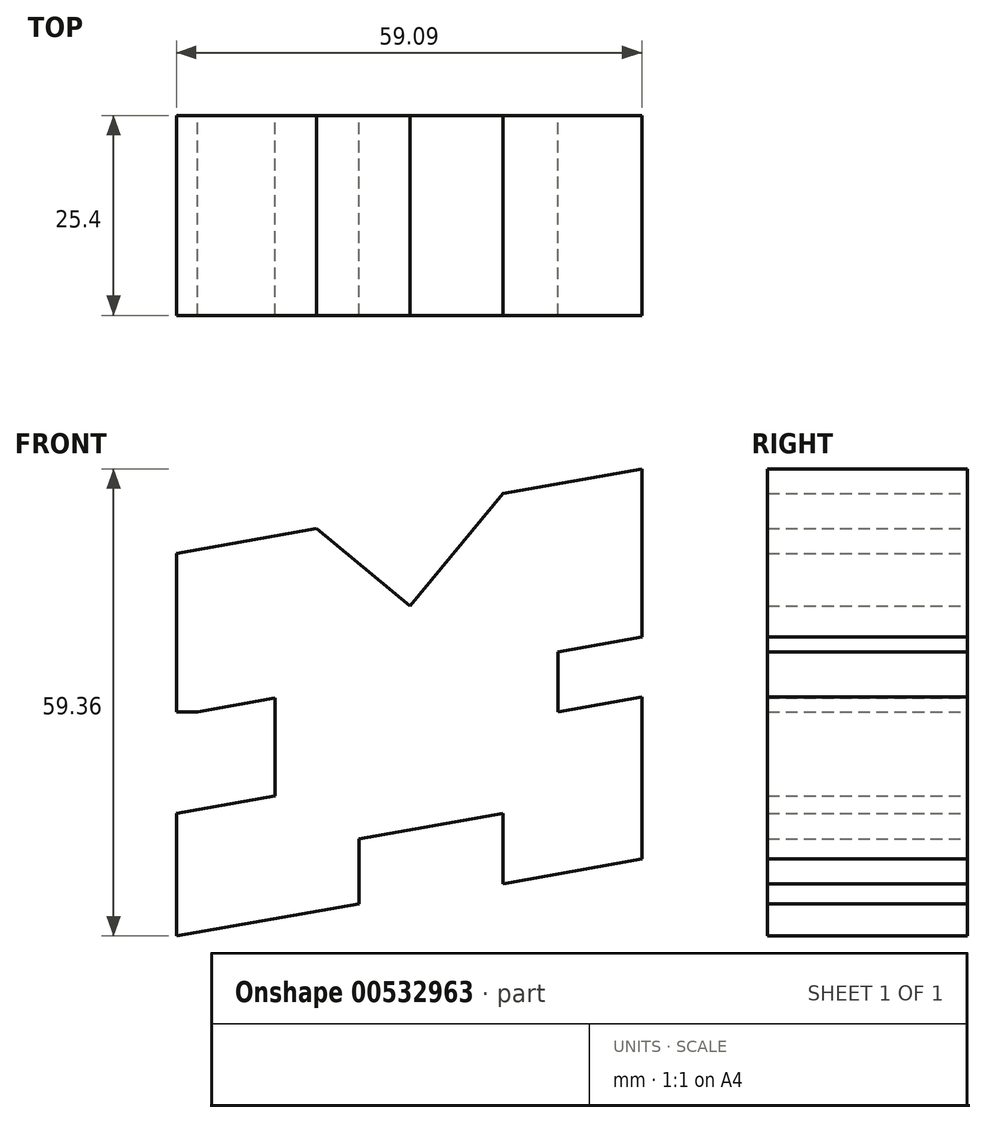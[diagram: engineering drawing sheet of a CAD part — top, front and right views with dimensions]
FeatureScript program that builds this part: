
annotation { "Feature Type Name" : "Feature", "Feature Type Description" : "" }
export const myFeature = defineFeature(function(context is Context, id is Id, definition is map)
    precondition{}
    {
        {
            var Q0;
            Q0=qCreatedBy(makeId("Front.planeOp"),FACE);
            var sketch = newSketch(context, id + "F0", { "sketchPlane" : qUnion([Q0])});
            skLineSegment(sketch, "E0", {"start": v(-29.68, 16.16) * mm, "end": v(-11.87, 19.33) * mm});
            skLineSegment(sketch, "E1", {"start": v(-11.87, 19.33) * mm, "end": v(0, 9.51) * mm});
            skLineSegment(sketch, "E2", {"start": v(0, 9.51) * mm, "end": v(11.78, 23.77) * mm});
            skLineSegment(sketch, "E3", {"start": v(11.78, 23.77) * mm, "end": v(29.41, 26.9) * mm});
            skLineSegment(sketch, "E4", {"start": v(-29.68, 16.16) * mm, "end": v(-29.68, -3.96) * mm});
            skLineSegment(sketch, "E5", {"start": v(29.41, 23.77) * mm, "end": v(29.41, 5.55) * mm});
            skLineSegment(sketch, "E6", {"start": v(-27.04, -3.96) * mm, "end": v(-17.17, -2.2) * mm});
            skLineSegment(sketch, "E7", {"start": v(-17.17, -2.2) * mm, "end": v(-17.17, -14.66) * mm});
            skLineSegment(sketch, "E8", {"start": v(-17.17, -14.66) * mm, "end": v(-29.68, -16.88) * mm});
            skLineSegment(sketch, "E9", {"start": v(-29.68, -16.88) * mm, "end": v(-29.68, -32.46) * mm});
            skLineSegment(sketch, "E10", {"start": v(-29.68, -32.46) * mm, "end": v(-6.52, -28.34) * mm});
            skLineSegment(sketch, "E11", {"start": v(29.41, 5.55) * mm, "end": v(18.75, 3.66) * mm});
            skLineSegment(sketch, "E12", {"start": v(18.75, 3.66) * mm, "end": v(18.75, -3.96) * mm});
            skLineSegment(sketch, "E13", {"start": v(18.75, -3.96) * mm, "end": v(29.41, -2.06) * mm});
            skLineSegment(sketch, "E14", {"start": v(29.41, -2.06) * mm, "end": v(29.41, -16.88) * mm});
            skLineSegment(sketch, "E15", {"start": v(29.41, -16.88) * mm, "end": v(29.41, -22.66) * mm});
            skPoint(sketch, "E15.endSnap0", {"position": v(29.41, -9.47) * mm});
            skLineSegment(sketch, "E16", {"start": v(29.41, -22.66) * mm, "end": v(11.78, -25.8) * mm});
            skLineSegment(sketch, "E17", {"start": v(11.78, -25.8) * mm, "end": v(11.78, -16.88) * mm});
            skLineSegment(sketch, "E18", {"start": v(11.78, -16.88) * mm, "end": v(-6.52, -20.13) * mm});
            skLineSegment(sketch, "E19", {"start": v(-6.52, -20.13) * mm, "end": v(-6.52, -28.34) * mm});
            skLineSegment(sketch, "E20", {"start": v(-27.04, -3.96) * mm, "end": v(-29.68, -3.96) * mm});
            skLineSegment(sketch, "E21", {"start": v(29.41, 26.9) * mm, "end": v(29.41, 19.33) * mm});
            skSolve(sketch);
        }
        {
            var Q0;
            Q0=makeQuery(id+"F0.imprint","IMPRINT",FACE,{"disambiguationData":[TD([[makeQuery(id+"F0.imprint","IMPRINT",EDGE,{"derivedFrom":sQuery(id+"F0.wireOp",EDGE,"E0")}),-1.0]])]});
            extrude(context, id + "F1", {"entities" : qUnion([Q0]), "depth" : 25.4 * mm, "offsetDistance" : 25.4 * mm});
        }
    });
